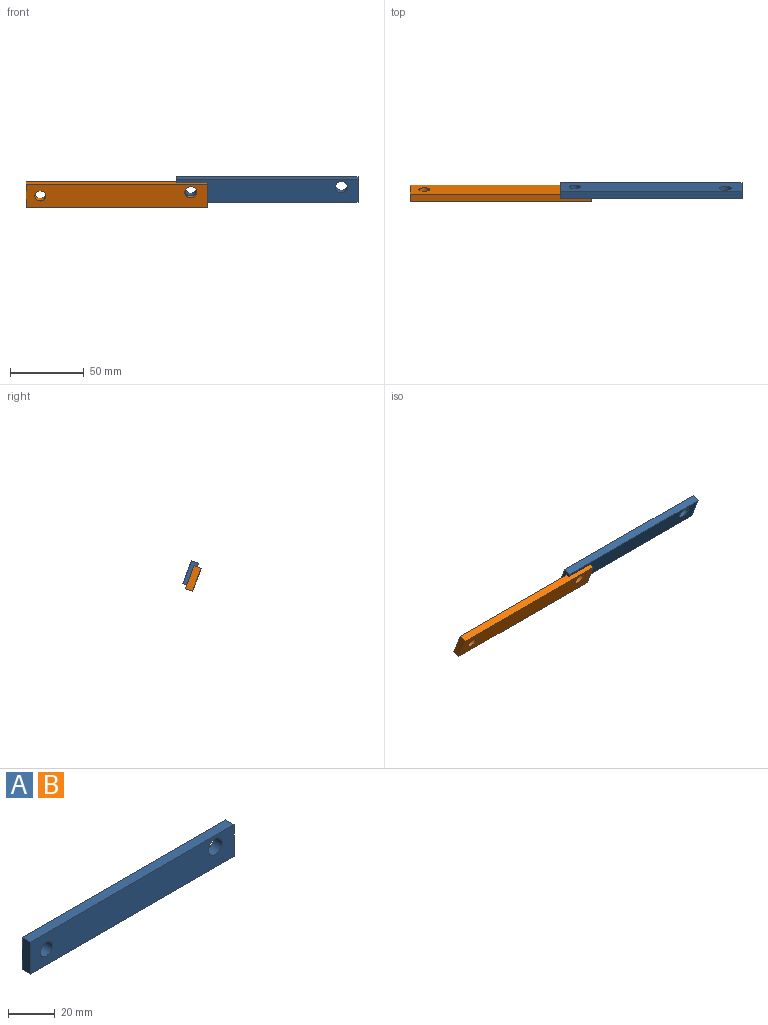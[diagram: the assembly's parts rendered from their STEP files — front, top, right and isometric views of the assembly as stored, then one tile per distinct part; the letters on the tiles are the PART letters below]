
ASSEMBLY  parts=2 mates=1
PART A: 8 faces, bbox 122.8x5.1x16.6 mm
  f0: plane 122.83x5.08mm, normal (0,0,1), area 624mm2, adj f1,f4,f6,f7
  f1: plane 16.61x5.08mm, normal (-1,0,0), area 84.4mm2, adj f0,f2,f6,f7
  f2: plane 122.83x5.08mm, normal (0,0,-1), area 624mm2, adj f1,f4,f6,f7
  f3: cylinder r=3.72mm len=7.45mm, axis (0,1,0), area 118.8mm2, adj f6,f7
  f4: plane 16.61x5.08mm, normal (1,0,0), area 84.4mm2, adj f0,f2,f6,f7
  f5: cylinder r=4.14mm len=8.29mm, axis (0,1,0), area 132.3mm2, adj f6,f7
  f6: plane 122.83x16.61mm, normal (0,-1,0), area 1942.8mm2, adj f0,f1,f2,f3,f4,f5
  f7: plane 122.83x16.61mm, normal (0,1,0), area 1942.8mm2, adj f0,f1,f2,f3,f4,f5
PART B: same geometry as A
PLACE A rot(axis=(1,0,0),20.9deg) t=(157.85,20.7,-1.02)mm
PLACE B rot(axis=(1,0,0),20.9deg) t=(55.96,18.98,-4.49)mm
MATE cylindrical B.f5 <-> A.f3  axis (0,-0.93,-0.36) through (104.57,-5.06,44.32)mm
